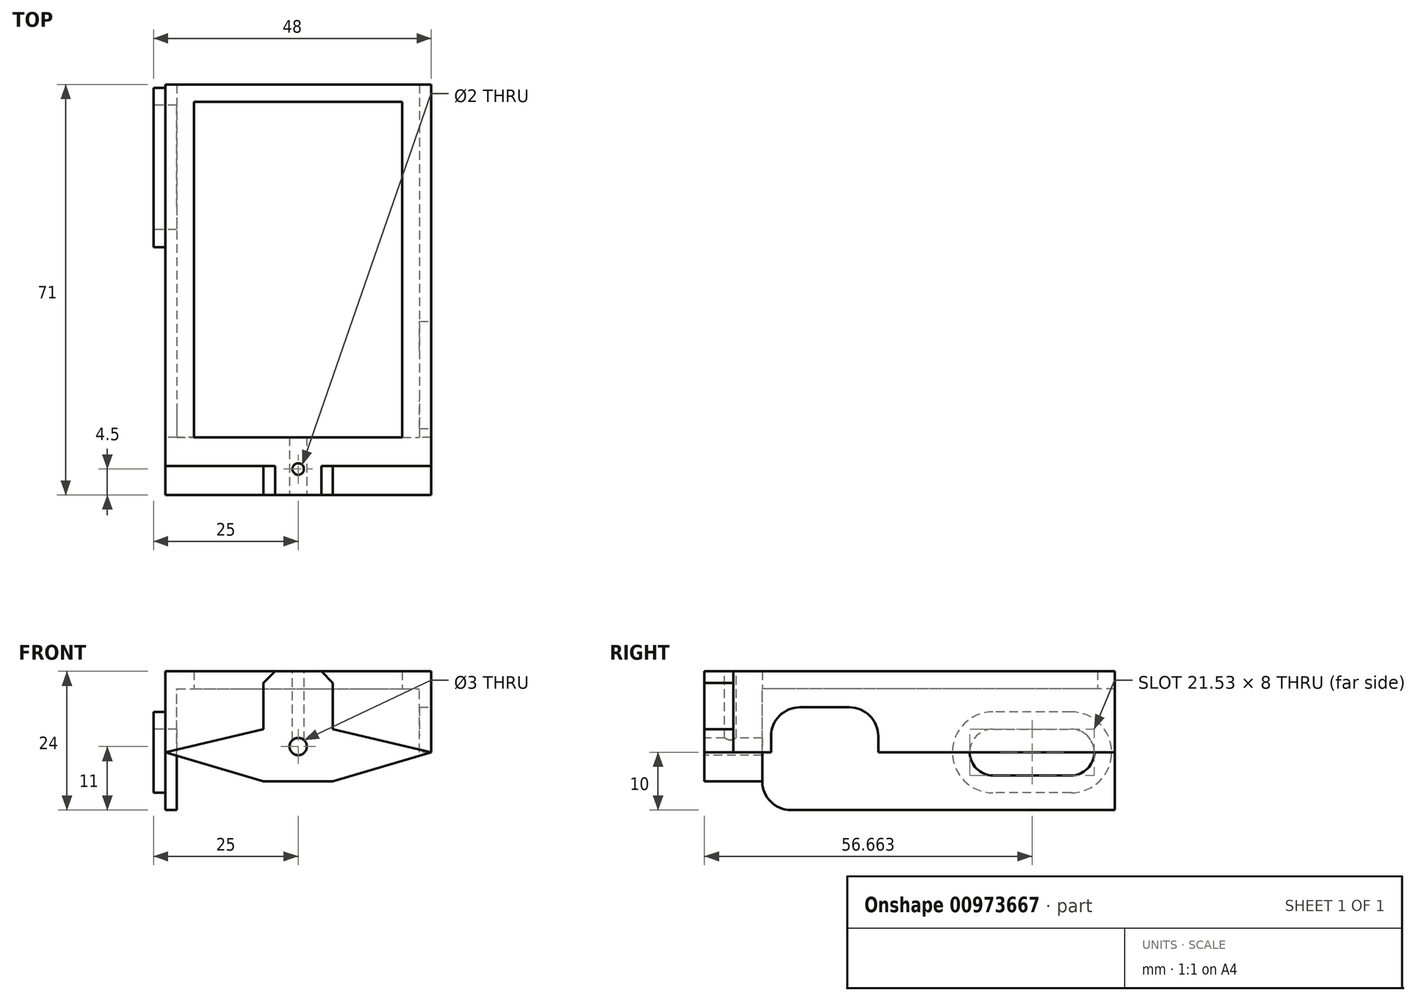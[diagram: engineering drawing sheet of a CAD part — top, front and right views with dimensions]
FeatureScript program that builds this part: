
annotation { "Feature Type Name" : "Feature", "Feature Type Description" : "" }
export const myFeature = defineFeature(function(context is Context, id is Id, definition is map)
    precondition{}
    {
        {
            var Q0;
            Q0=qCreatedBy(makeId("Top.planeOp"),FACE);
            var sketch = newSketch(context, id + "F0", { "sketchPlane" : qUnion([Q0])});
            skLineSegment(sketch, "E0.bottom", {"start": v(-23, -33) * mm, "end": v(23, -33) * mm});
            skLineSegment(sketch, "E0.top", {"start": v(-23, 33) * mm, "end": v(23, 33) * mm});
            skLineSegment(sketch, "E0.left", {"start": v(-23, -33) * mm, "end": v(-23, 33) * mm});
            skLineSegment(sketch, "E0.right", {"start": v(23, -33) * mm, "end": v(23, 33) * mm});
            skPoint(sketch, "E0.middle", {"position": v(0, 0) * mm});
            skLineSegment(sketch, "E1.bottom", {"start": v(-18, 30) * mm, "end": v(18, 30) * mm});
            skLineSegment(sketch, "E1.top", {"start": v(-18, -28) * mm, "end": v(18, -28) * mm});
            skLineSegment(sketch, "E1.left", {"start": v(-18, 30) * mm, "end": v(-18, -28) * mm});
            skLineSegment(sketch, "E1.right", {"start": v(18, 30) * mm, "end": v(18, -28) * mm});
            skSolve(sketch);
        }
        {
            var Q0;
            Q0=makeQuery(id+"F0.imprint","IMPRINT",FACE,{"disambiguationData":[TD([[makeQuery(id+"F0.imprint","IMPRINT",EDGE,{"derivedFrom":sQuery(id+"F0.wireOp",EDGE,"E0.bottom")}),1.0]])]});
            extrude(context, id + "F1", {"entities" : qUnion([Q0]), "depth" : 3 * mm, "offsetDistance" : 25 * mm});
        }
        {
            var Q0;
            Q0=makeQuery(id+"F1.opExtrude","CAP_FACE",FACE,{"disambiguationData":[OSD([sQuery(id+"F0.wireOp",EDGE,"E0.bottom"),sQuery(id+"F0.wireOp",EDGE,"E0.top"),sQuery(id+"F0.wireOp",EDGE,"E0.left"),sQuery(id+"F0.wireOp",EDGE,"E0.right"),sQuery(id+"F0.wireOp",EDGE,"E1.bottom"),sQuery(id+"F0.wireOp",EDGE,"E1.top"),sQuery(id+"F0.wireOp",EDGE,"E1.left"),sQuery(id+"F0.wireOp",EDGE,"E1.right")])],"isStart":true});
            var sketch = newSketch(context, id + "F2", { "sketchPlane" : qUnion([Q0])});
            skLineSegment(sketch, "E2.bottom", {"start": v(23, -33) * mm, "end": v(21, -33) * mm});
            skLineSegment(sketch, "E2.top", {"start": v(23, 33) * mm, "end": v(21, 33) * mm});
            skLineSegment(sketch, "E2.left", {"start": v(23, -33) * mm, "end": v(23, 33) * mm});
            skLineSegment(sketch, "E2.right", {"start": v(21, -33) * mm, "end": v(21, 33) * mm});
            skLineSegment(sketch, "E3.bottom", {"start": v(-23, 28) * mm, "end": v(23, 28) * mm});
            skLineSegment(sketch, "E3.top", {"start": v(-23, 33) * mm, "end": v(23, 33) * mm});
            skLineSegment(sketch, "E3.left", {"start": v(-23, 28) * mm, "end": v(-23, 33) * mm});
            skLineSegment(sketch, "E3.right", {"start": v(23, 28) * mm, "end": v(23, 33) * mm});
            skLineSegment(sketch, "E4.bottom", {"start": v(-23, -33) * mm, "end": v(-21, -33) * mm});
            skLineSegment(sketch, "E4.top", {"start": v(-23, 28) * mm, "end": v(-21, 28) * mm});
            skLineSegment(sketch, "E4.left", {"start": v(-23, -33) * mm, "end": v(-23, 28) * mm});
            skLineSegment(sketch, "E4.right", {"start": v(-21, -33) * mm, "end": v(-21, 28) * mm});
            skSolve(sketch);
        }
        {
            var Q0;
            Q0=makeQuery(id+"F2.imprint","IMPRINT",FACE,{"disambiguationData":[TD([[makeQuery(id+"F2.imprint","IMPRINT",EDGE,{"derivedFrom":sQuery(id+"F2.wireOp",EDGE,"E4.bottom")}),1.0]])]});
            var Q1;
            {var subQ5=sQuery(id+"F2.wireOp",EDGE,"E3.top");Q1=makeQuery(id+"F2.imprint","IMPRINT",FACE,{"disambiguationData":[TD([[makeQuery(id+"F2.imprint","IMPRINT",EDGE,{"derivedFrom":subQ5}),-1.0]])]});}
            var Q2;
            {var subQ0=sQuery(id+"F2.wireOp",EDGE,"E2.bottom");Q2=makeQuery(id+"F2.imprint","IMPRINT",FACE,{"disambiguationData":[TD([[makeQuery(id+"F2.imprint","IMPRINT",EDGE,{"derivedFrom":subQ0}),1.0]])]});}
            var Q3;
            {var subQ0=sQuery(id+"F2.wireOp",EDGE,"E2.top");Q3=makeQuery(id+"F2.imprint","IMPRINT",FACE,{"disambiguationData":[TD([[makeQuery(id+"F2.imprint","IMPRINT",EDGE,{"derivedFrom":subQ0}),-1.0]])]});}
            extrude(context, id + "F3", {"entities" : qUnion([Q0, Q1, Q2, Q3]), "operationType" : NewBodyOperationType.ADD, "depth" : 11 * mm, "offsetDistance" : 25 * mm});
        }
        {
            var Q0;
            Q0=makeQuery(id+"F3.boolean.opBoolean","MERGE",FACE,{"derivedFrom":[makeQuery(id+"F1.opExtrude","SWEPT_FACE",FACE,{"disambiguationData":[OSD([sQuery(id+"F0.wireOp",EDGE,"E0.right")])]}),makeQuery(id+"F3.opExtrude","SWEPT_FACE",FACE,{"disambiguationData":[OSD([sQuery(id+"F2.wireOp",EDGE,"E2.left")])]})]});
            var sketch = newSketch(context, id + "F4", { "sketchPlane" : qUnion([Q0])});
            skLineSegment(sketch, "E5.bottom", {"start": v(-7.94, -11) * mm, "end": v(-26.47, -11) * mm});
            skLineSegment(sketch, "E5.top", {"start": v(-12.94, -3.21) * mm, "end": v(-21.47, -3.21) * mm});
            skLineSegment(sketch, "E5.left", {"start": v(-7.94, -11) * mm, "end": v(-7.94, -8.21) * mm});
            skLineSegment(sketch, "E5.right", {"start": v(-26.47, -11) * mm, "end": v(-26.47, -8.21) * mm});
            skPoint(sketch, "E6.visualSharp", {"position": v(-7.94, -3.21) * mm});
            skArc(sketch, "E6.filletArc", {"start": v(-7.94, -8.21) * mm, "mid": v(-9.4, -4.68) * mm, "end": v(-12.94, -3.21) * mm});
            skPoint(sketch, "E7.visualSharp", {"position": v(-26.47, -3.21) * mm});
            skArc(sketch, "E7.filletArc", {"start": v(-21.47, -3.21) * mm, "mid": v(-25, -4.68) * mm, "end": v(-26.47, -8.21) * mm});
            skSolve(sketch);
        }
        {
            var Q0;
            Q0=makeQuery(id+"F4.imprint","IMPRINT",FACE,{"disambiguationData":[TD([[makeQuery(id+"F4.imprint","IMPRINT",EDGE,{"derivedFrom":sQuery(id+"F4.wireOp",EDGE,"E5.bottom")}),1.0]])]});
            extrude(context, id + "F5", {"entities" : qUnion([Q0]), "operationType" : NewBodyOperationType.REMOVE, "endBound" : BoundingType.UP_TO_NEXT, "oppositeDirection" : true, "depth" : 25 * mm, "offsetDistance" : 25 * mm});
        }
        {
            var Q0;
            Q0=makeQuery(id+"F3.boolean.opBoolean","MERGE",FACE,{"derivedFrom":[makeQuery(id+"F1.opExtrude","SWEPT_FACE",FACE,{"disambiguationData":[OSD([sQuery(id+"F0.wireOp",EDGE,"E0.bottom")])]}),makeQuery(id+"F3.opExtrude","SWEPT_FACE",FACE,{"disambiguationData":[OSD([sQuery(id+"F2.wireOp",EDGE,"E2.top"),sQuery(id+"F2.wireOp",EDGE,"E3.top")])]})]});
            var sketch = newSketch(context, id + "F6", { "sketchPlane" : qUnion([Q0])});
            skLineSegment(sketch, "E8.bottom", {"start": v(6, 3) * mm, "end": v(-6, 3) * mm});
            skLineSegment(sketch, "E8.top", {"start": v(6, -7) * mm, "end": v(-6, -7) * mm});
            skLineSegment(sketch, "E8.left", {"start": v(6, 3) * mm, "end": v(6, -7) * mm});
            skLineSegment(sketch, "E8.right", {"start": v(-6, 3) * mm, "end": v(-6, -7) * mm});
            skLineSegment(sketch, "E9", {"start": v(-23, -11) * mm, "end": v(-6, -7) * mm});
            skLineSegment(sketch, "E10", {"start": v(6, -7) * mm, "end": v(23, -11) * mm});
            skLineSegment(sketch, "E11", {"start": v(23, -11) * mm, "end": v(6, -16) * mm});
            skLineSegment(sketch, "E12", {"start": v(6, -16) * mm, "end": v(-6, -16) * mm});
            skLineSegment(sketch, "E13", {"start": v(-6, -16) * mm, "end": v(-23, -11) * mm});
            skLineSegment(sketch, "E14", {"start": v(-6, -1.22) * mm, "end": v(-23, -1.22) * mm, "construction": true});
            skLineSegment(sketch, "E15", {"start": v(6, -1.15) * mm, "end": v(23, -1.15) * mm, "construction": true});
            skSolve(sketch);
        }
        {
            var Q0;
            Q0 = qSketchRegion(id + "F6", true);
            extrude(context, id + "F7", {"entities" : qUnion([Q0]), "operationType" : NewBodyOperationType.ADD, "depth" : 5 * mm, "offsetDistance" : 25 * mm, "hasSecondDirection" : true, "secondDirectionOppositeDirection" : true, "secondDirectionDepth" : 5 * mm});
        }
        {
            var Q0;
            Q0=makeQuery(id+"F7.opExtrude","CAP_FACE",FACE,{"disambiguationData":[OSD([sQuery(id+"F6.wireOp",EDGE,"E8.bottom"),sQuery(id+"F6.wireOp",EDGE,"E8.left"),sQuery(id+"F6.wireOp",EDGE,"E8.right"),sQuery(id+"F6.wireOp",EDGE,"E9"),sQuery(id+"F6.wireOp",EDGE,"E10"),sQuery(id+"F6.wireOp",EDGE,"E11"),sQuery(id+"F6.wireOp",EDGE,"E12"),sQuery(id+"F6.wireOp",EDGE,"E13")])],"isStart":false});
            var sketch = newSketch(context, id + "F8", { "sketchPlane" : qUnion([Q0])});
            skCircle(sketch, "E16", {"center": v(0, -10) * mm, "radius": 1.5 * mm});
            skPoint(sketch, "E16.centerSnap0", {"position": v(0, -16) * mm});
            skSolve(sketch);
        }
        {
            var Q0;
            Q0 = qSketchRegion(id + "F8", true);
            extrude(context, id + "F9", {"entities" : qUnion([Q0]), "operationType" : NewBodyOperationType.REMOVE, "endBound" : BoundingType.UP_TO_NEXT, "oppositeDirection" : true, "depth" : 25 * mm, "offsetDistance" : 25 * mm});
        }
        {
            var Q0;
            Q0=makeQuery(id+"F7.boolean.opBoolean","MERGE",FACE,{"derivedFrom":[makeQuery(id+"F1.opExtrude","CAP_FACE",FACE,{"disambiguationData":[OSD([sQuery(id+"F0.wireOp",EDGE,"E0.bottom"),sQuery(id+"F0.wireOp",EDGE,"E0.top"),sQuery(id+"F0.wireOp",EDGE,"E0.left"),sQuery(id+"F0.wireOp",EDGE,"E0.right"),sQuery(id+"F0.wireOp",EDGE,"E1.bottom"),sQuery(id+"F0.wireOp",EDGE,"E1.top"),sQuery(id+"F0.wireOp",EDGE,"E1.left"),sQuery(id+"F0.wireOp",EDGE,"E1.right")])],"isStart":false}),makeQuery(id+"F7.opExtrude","SWEPT_FACE",FACE,{"disambiguationData":[OSD([sQuery(id+"F6.wireOp",EDGE,"E8.bottom")])]})]});
            var sketch = newSketch(context, id + "F10", { "sketchPlane" : qUnion([Q0])});
            skCircle(sketch, "E17", {"center": v(0, -33.5) * mm, "radius": 1 * mm});
            skPoint(sketch, "E17.centerSnap0", {"position": v(0, -38) * mm});
            skSolve(sketch);
        }
        {
            var Q0;
            Q0 = qSketchRegion(id + "F10", true);
            extrude(context, id + "F11", {"entities" : qUnion([Q0]), "operationType" : NewBodyOperationType.REMOVE, "endBound" : BoundingType.UP_TO_NEXT, "oppositeDirection" : true, "depth" : 25 * mm, "offsetDistance" : 25 * mm});
        }
        {
            var Q0;
            {var subQ1=sQuery(id+"F2.wireOp",EDGE,"E3.bottom");var subQ4=sQuery(id+"F2.wireOp",EDGE,"E2.bottom");var subQ7=makeQuery(id+"F1.opExtrude","SWEPT_FACE",FACE,{"disambiguationData":[OSD([sQuery(id+"F0.wireOp",EDGE,"E0.top")])]});var subQ8=sQuery(id+"F2.wireOp",EDGE,"E4.left");var subQ9=sQuery(id+"F2.wireOp",EDGE,"E3.left");var subQ11=sQuery(id+"F2.wireOp",EDGE,"E4.bottom");var subQ13=sQuery(id+"F2.wireOp",EDGE,"E4.right");var subQ15=sQuery(id+"F2.wireOp",EDGE,"E2.right");var subQ16=sQuery(id+"F2.wireOp",EDGE,"E3.top");var subQ17=sQuery(id+"F2.wireOp",EDGE,"E2.top");var subQ18=sQuery(id+"F2.wireOp",EDGE,"E2.left");Q0=makeQuery(id+"F7.boolean.opBoolean","SPLIT",FACE,{"disambiguationData":[TD([subQ7])],"derivedFrom":makeQuery(id+"F5.boolean.opBoolean","SPLIT",FACE,{"disambiguationData":[TD([makeQuery(id+"F1.opExtrude","SWEPT_FACE",FACE,{"disambiguationData":[OSD([sQuery(id+"F0.wireOp",EDGE,"E0.bottom")])]})])],"derivedFrom":makeQuery(id+"F3.opExtrude","CAP_FACE",FACE,{"disambiguationData":[OSD([subQ4,subQ17,subQ18,subQ15,subQ1,subQ16,subQ9,subQ11,subQ8,subQ13])],"isStart":false})})});}
            extrude(context, id + "F12", {"entities" : qUnion([Q0]), "operationType" : NewBodyOperationType.ADD, "depth" : 10 * mm, "offsetDistance" : 25 * mm});
        }
        {
            var Q0;
            {var subQ0=sQuery(id+"F2.wireOp",EDGE,"E4.left");var subQ1=sQuery(id+"F2.wireOp",EDGE,"E3.left");Q0=makeQuery(id+"F12.boolean.opBoolean","MERGE",FACE,{"derivedFrom":[makeQuery(id+"F3.boolean.opBoolean","MERGE",FACE,{"derivedFrom":[makeQuery(id+"F1.opExtrude","SWEPT_FACE",FACE,{"disambiguationData":[OSD([sQuery(id+"F0.wireOp",EDGE,"E0.left")])]}),makeQuery(id+"F3.opExtrude","SWEPT_FACE",FACE,{"disambiguationData":[OSD([subQ1,subQ0])]})]}),makeQuery(id+"F12.opExtrude","SWEPT_FACE",FACE,{"disambiguationData":[OSD([subQ1,subQ0])]})]});}
            var sketch = newSketch(context, id + "F13", { "sketchPlane" : qUnion([Q0])});
            skLineSegment(sketch, "E18", {"start": v(-25.43, -11) * mm, "end": v(-11.9, -11) * mm});
            skArc(sketch, "E19.0.startCap", {"start": v(-25.43, -15) * mm, "mid": v(-29.43, -11) * mm, "end": v(-25.43, -7) * mm});
            skArc(sketch, "E19.0.endCap", {"start": v(-11.9, -7) * mm, "mid": v(-7.9, -11) * mm, "end": v(-11.9, -15) * mm});
            skLineSegment(sketch, "E19.0.left", {"start": v(-25.43, -7) * mm, "end": v(-11.9, -7) * mm});
            skLineSegment(sketch, "E19.0.right", {"start": v(-25.43, -15) * mm, "end": v(-11.9, -15) * mm});
            skSolve(sketch);
        }
        {
            var Q0;
            Q0 = qSketchRegion(id + "F13", true);
            extrude(context, id + "F14", {"entities" : qUnion([Q0]), "operationType" : NewBodyOperationType.REMOVE, "endBound" : BoundingType.UP_TO_NEXT, "oppositeDirection" : true, "depth" : 25 * mm, "offsetDistance" : 25 * mm});
        }
        {
            var Q0;
            {var subQ0=sQuery(id+"F2.wireOp",EDGE,"E4.left");var subQ1=sQuery(id+"F2.wireOp",EDGE,"E3.left");Q0=makeQuery(id+"F12.boolean.opBoolean","MERGE",FACE,{"derivedFrom":[makeQuery(id+"F3.boolean.opBoolean","MERGE",FACE,{"derivedFrom":[makeQuery(id+"F1.opExtrude","SWEPT_FACE",FACE,{"disambiguationData":[OSD([sQuery(id+"F0.wireOp",EDGE,"E0.left")])]}),makeQuery(id+"F3.opExtrude","SWEPT_FACE",FACE,{"disambiguationData":[OSD([subQ1,subQ0])]})]}),makeQuery(id+"F12.opExtrude","SWEPT_FACE",FACE,{"disambiguationData":[OSD([subQ1,subQ0])]})]});}
            var sketch = newSketch(context, id + "F15", { "sketchPlane" : qUnion([Q0])});
            skLineSegment(sketch, "E20.0", {"start": v(-25.43, -15) * mm, "end": v(-11.9, -15) * mm});
            skArc(sketch, "E20.1", {"start": v(-11.9, -7) * mm, "mid": v(-7.9, -11) * mm, "end": v(-11.9, -15) * mm});
            skLineSegment(sketch, "E20.2", {"start": v(-25.43, -7) * mm, "end": v(-11.9, -7) * mm});
            skArc(sketch, "E20.3", {"start": v(-25.43, -15) * mm, "mid": v(-29.43, -11) * mm, "end": v(-25.43, -7) * mm});
            skLineSegment(sketch, "E21.0", {"start": v(-25.43, -18) * mm, "end": v(-11.9, -18) * mm});
            skArc(sketch, "E21.1", {"start": v(-25.43, -18) * mm, "mid": v(-32.43, -11) * mm, "end": v(-25.43, -4) * mm});
            skLineSegment(sketch, "E21.2", {"start": v(-25.43, -4) * mm, "end": v(-11.9, -4) * mm});
            skArc(sketch, "E21.3", {"start": v(-11.9, -4) * mm, "mid": v(-4.9, -11) * mm, "end": v(-11.9, -18) * mm});
            skSolve(sketch);
        }
        {
            var Q0;
            Q0 = qSketchRegion(id + "F15", true);
            extrude(context, id + "F16", {"entities" : qUnion([Q0]), "operationType" : NewBodyOperationType.ADD, "depth" : 2 * mm, "offsetDistance" : 25 * mm});
        }
        {
            var Q0;
            Q0=makeQuery(id+"F12.opExtrude","CAP_EDGE",EDGE,{"disambiguationData":[OSD([sQuery(id+"F2.wireOp",EDGE,"E2.bottom"),sQuery(id+"F2.wireOp",EDGE,"E2.top"),sQuery(id+"F2.wireOp",EDGE,"E2.left"),sQuery(id+"F2.wireOp",EDGE,"E2.right"),sQuery(id+"F2.wireOp",EDGE,"E3.bottom"),sQuery(id+"F2.wireOp",EDGE,"E3.top"),sQuery(id+"F2.wireOp",EDGE,"E3.left"),sQuery(id+"F2.wireOp",EDGE,"E4.bottom"),sQuery(id+"F2.wireOp",EDGE,"E4.left"),sQuery(id+"F2.wireOp",EDGE,"E4.right"),sQuery(id+"F6.wireOp",EDGE,"E8.bottom"),sQuery(id+"F6.wireOp",EDGE,"E8.left"),sQuery(id+"F6.wireOp",EDGE,"E8.right"),sQuery(id+"F6.wireOp",EDGE,"E9"),sQuery(id+"F6.wireOp",EDGE,"E10"),sQuery(id+"F6.wireOp",EDGE,"E11"),sQuery(id+"F6.wireOp",EDGE,"E12"),sQuery(id+"F6.wireOp",EDGE,"E13")])],"isStart":false});
            fillet(context, id + "F17", {"entities" : qUnion([Q0]), "radius" : 5 * mm, "tangentPropagation" : true, "allowEdgeOverflow" : false});
        }
        {
            var Q0;
            Q0=makeQuery(id+"F7.opExtrude","SWEPT_EDGE",EDGE,{"disambiguationData":[OSD([sQuery(id+"F0.wireOp",EDGE,"E0.bottom"),sQuery(id+"F6.wireOp",EDGE,"E8.bottom"),sQuery(id+"F6.wireOp",EDGE,"E8.left")])]});
            var Q1;
            Q1=makeQuery(id+"F7.opExtrude","SWEPT_EDGE",EDGE,{"disambiguationData":[OSD([sQuery(id+"F0.wireOp",EDGE,"E0.bottom"),sQuery(id+"F6.wireOp",EDGE,"E8.bottom"),sQuery(id+"F6.wireOp",EDGE,"E8.right")])]});
            chamfer(context, id + "F18", {"entities" : qUnion([Q0, Q1]), "width" : 2 * mm, "tangentPropagation" : true});
        }
    });
